# Revit family: PRD_FrankeWS_SnksSuprts_FeetForPlasterSink_SIRX838
name_source: partatom
category: Plumbing Fixtures
revit_build: Autodesk Revit 2018 (Build: 20190510_1515(x64)
units: mm (PartAtom-declared; Revit-internal decimal feet)

## family parameters
Always vertical = No
Cut with Voids When Loaded = No
OmniClass Number = 23.40.20.21
OmniClass Title = Toilet and Bath Specialties
Part Type = Normal
Room Calculation Point = No
Round Connector Dimension = Use Diameter
Shared = Yes
Work Plane-Based = No

## types (3) — shared parameters
AssetType = Fixed
BIMObjectName = PRD_AR_SinkSupports_FeetForPlasterSink_SIRX838
BracketMaterial = PRD_AR_StainlessSteel_SatinFinished
Category = Pr_20_85_09_88, Sink supports
Color = Stainless steel
Description = Feet for plaster sink, stainless steel.
Dimensions = 30 x 820 x 580 mm
DurationUnit = year
Features = stainless steel
Finish = Satin finished
GrossWeight = 3.90 kg
IfcExportAs = IfcBuildingElementProxy
IfcExportType = NOTDEFINED
Manufacturer = KWC Group AG
ManufacturerName = KWC Group AG
ManufacturerURL = www.kwc.com
Material = Stainless steel
MaterialCode = stainless steel
stainless steel
MaterialsBracketsBody = Stainless steel 1.4301
MaterialsBracketsFinishAndColour = Satin finished
MaterialsLegsBody = stainless steel
Model = SIRX838
ModelNumber = 2000103301
ModelReference = SIRX838
NBSDescription = Supports for sinks
NBSReference = 45-35-70/347
Name = Feet for plaster sink, SIRX838
NetWeight = 2.80 kg
NominalHeight = 580 mm  [stored 1.90289 ft]
NominalLength = 30 mm  [stored 0.0984252 ft]
NominalWidth = 820 mm  [stored 2.69029 ft]
ProductInformation = https://pim.kwc.com
URL = www.kwc.com
Uniclass2015Code = Pr_20_85_09_88
Uniclass2015Title = Sink supports
Uniclass2015Version = Products v1.7
Version = 1
WarrantyDurationUnit = year

## per-type parameters (varying)
| type | 2pcs left | 2pcs right | left | right |
| SIRX838 1pce left | No | No | Yes | No |
| SIRX838 1pce right | No | No | No | Yes |
| SIRX838 2 pieces | Yes | Yes | No | No |

note: [stored X ft] marks values corroborated as IEEE doubles in the binary element streams (Revit-internal decimal feet)

## geometry (parser evidence)
native form markers: Sweep x3
no freeform markers — native parametric forms only
